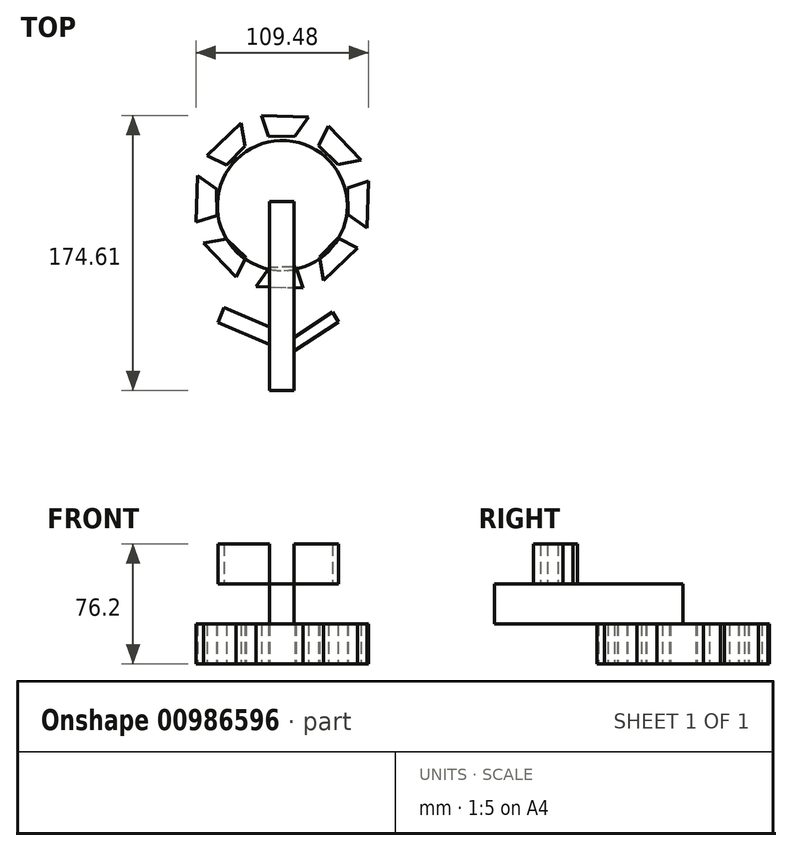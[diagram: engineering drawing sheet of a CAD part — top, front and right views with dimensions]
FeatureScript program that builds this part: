
annotation { "Feature Type Name" : "Feature", "Feature Type Description" : "" }
export const myFeature = defineFeature(function(context is Context, id is Id, definition is map)
    precondition{}
    {
        {
            var Q0;
            Q0=qCreatedBy(makeId("Top.planeOp"),FACE);
            var sketch = newSketch(context, id + "F0", { "sketchPlane" : qUnion([Q0])});
            skCircle(sketch, "E0", {"center": v(0, -2.45) * mm, "radius": 41.29 * mm});
            skSolve(sketch);
        }
        {
            var Q0;
            Q0=qCreatedBy(makeId("Top.planeOp"),FACE);
            var sketch = newSketch(context, id + "F1", { "sketchPlane" : qUnion([Q0])});
            skLineSegment(sketch, "E1", {"start": v(23.17, 35.54) * mm, "end": v(35.26, 23.74) * mm});
            skLineSegment(sketch, "E2", {"start": v(35.26, 23.74) * mm, "end": v(49.93, 26.33) * mm});
            skLineSegment(sketch, "E3", {"start": v(49.93, 26.33) * mm, "end": v(29.5, 47.92) * mm});
            skLineSegment(sketch, "E4", {"start": v(29.5, 47.92) * mm, "end": v(23.17, 35.54) * mm});
            skLineSegment(sketch, "E5.1.0", {"start": v(-13.02, 54.74) * mm, "end": v(-8.75, 41.52) * mm});
            skLineSegment(sketch, "E5.1.1", {"start": v(16.69, 53.93) * mm, "end": v(-13.02, 54.74) * mm});
            skLineSegment(sketch, "E5.1.2", {"start": v(8.14, 41.72) * mm, "end": v(16.69, 53.93) * mm});
            skLineSegment(sketch, "E5.1.3", {"start": v(-8.75, 41.52) * mm, "end": v(8.14, 41.72) * mm});
            skLineSegment(sketch, "E5.2.0", {"start": v(-47.92, 29.5) * mm, "end": v(-35.54, 23.17) * mm});
            skLineSegment(sketch, "E5.2.1", {"start": v(-26.33, 49.93) * mm, "end": v(-47.92, 29.5) * mm});
            skLineSegment(sketch, "E5.2.2", {"start": v(-23.74, 35.26) * mm, "end": v(-26.33, 49.93) * mm});
            skLineSegment(sketch, "E5.2.3", {"start": v(-35.54, 23.17) * mm, "end": v(-23.74, 35.26) * mm});
            skLineSegment(sketch, "E5.3.0", {"start": v(-54.74, -13.02) * mm, "end": v(-41.52, -8.75) * mm});
            skLineSegment(sketch, "E5.3.1", {"start": v(-53.93, 16.69) * mm, "end": v(-54.74, -13.02) * mm});
            skLineSegment(sketch, "E5.3.2", {"start": v(-41.72, 8.14) * mm, "end": v(-53.93, 16.69) * mm});
            skLineSegment(sketch, "E5.3.3", {"start": v(-41.52, -8.75) * mm, "end": v(-41.72, 8.14) * mm});
            skLineSegment(sketch, "E5.4.0", {"start": v(-29.5, -47.92) * mm, "end": v(-23.17, -35.54) * mm});
            skLineSegment(sketch, "E5.4.1", {"start": v(-49.93, -26.33) * mm, "end": v(-29.5, -47.92) * mm});
            skLineSegment(sketch, "E5.4.2", {"start": v(-35.26, -23.74) * mm, "end": v(-49.93, -26.33) * mm});
            skLineSegment(sketch, "E5.4.3", {"start": v(-23.17, -35.54) * mm, "end": v(-35.26, -23.74) * mm});
            skLineSegment(sketch, "E5.5.0", {"start": v(13.02, -54.74) * mm, "end": v(8.75, -41.52) * mm});
            skLineSegment(sketch, "E5.5.1", {"start": v(-16.69, -53.93) * mm, "end": v(13.02, -54.74) * mm});
            skLineSegment(sketch, "E5.5.2", {"start": v(-8.14, -41.72) * mm, "end": v(-16.69, -53.93) * mm});
            skLineSegment(sketch, "E5.5.3", {"start": v(8.75, -41.52) * mm, "end": v(-8.14, -41.72) * mm});
            skLineSegment(sketch, "E5.6.0", {"start": v(47.92, -29.5) * mm, "end": v(35.54, -23.17) * mm});
            skLineSegment(sketch, "E5.6.1", {"start": v(26.33, -49.93) * mm, "end": v(47.92, -29.5) * mm});
            skLineSegment(sketch, "E5.6.2", {"start": v(23.74, -35.26) * mm, "end": v(26.33, -49.93) * mm});
            skLineSegment(sketch, "E5.6.3", {"start": v(35.54, -23.17) * mm, "end": v(23.74, -35.26) * mm});
            skLineSegment(sketch, "E5.7.0", {"start": v(54.74, 13.02) * mm, "end": v(41.52, 8.75) * mm});
            skLineSegment(sketch, "E5.7.1", {"start": v(53.93, -16.69) * mm, "end": v(54.74, 13.02) * mm});
            skLineSegment(sketch, "E5.7.2", {"start": v(41.72, -8.14) * mm, "end": v(53.93, -16.69) * mm});
            skLineSegment(sketch, "E5.7.3", {"start": v(41.52, 8.75) * mm, "end": v(41.72, -8.14) * mm});
            skPoint(sketch, "E5.center", {"position": v(0, 0) * mm});
            skSolve(sketch);
        }
        {
            var Q0;
            Q0=makeQuery(id+"F1.imprint","IMPRINT",FACE,{"disambiguationData":[TD([[makeQuery(id+"F1.imprint","IMPRINT",EDGE,{"derivedFrom":sQuery(id+"F1.wireOp",EDGE,"E5.6.0")}),1.0]])]});
            var Q1;
            Q1=makeQuery(id+"F1.imprint","IMPRINT",FACE,{"disambiguationData":[TD([[makeQuery(id+"F1.imprint","IMPRINT",EDGE,{"derivedFrom":sQuery(id+"F1.wireOp",EDGE,"E5.7.0")}),1.0]])]});
            var Q2;
            Q2=makeQuery(id+"F1.imprint","IMPRINT",FACE,{"disambiguationData":[TD([[makeQuery(id+"F1.imprint","IMPRINT",EDGE,{"derivedFrom":sQuery(id+"F1.wireOp",EDGE,"E5.1.0")}),1.0]])]});
            var Q3;
            Q3=makeQuery(id+"F1.imprint","IMPRINT",FACE,{"disambiguationData":[TD([[makeQuery(id+"F1.imprint","IMPRINT",EDGE,{"derivedFrom":sQuery(id+"F1.wireOp",EDGE,"E5.2.0")}),1.0]])]});
            var Q4;
            Q4=makeQuery(id+"F1.imprint","IMPRINT",FACE,{"disambiguationData":[TD([[makeQuery(id+"F1.imprint","IMPRINT",EDGE,{"derivedFrom":sQuery(id+"F1.wireOp",EDGE,"E5.3.0")}),1.0]])]});
            var Q5;
            Q5=makeQuery(id+"F1.imprint","IMPRINT",FACE,{"disambiguationData":[TD([[makeQuery(id+"F1.imprint","IMPRINT",EDGE,{"derivedFrom":sQuery(id+"F1.wireOp",EDGE,"E5.4.0")}),1.0]])]});
            var Q6;
            Q6=makeQuery(id+"F1.imprint","IMPRINT",FACE,{"disambiguationData":[TD([[makeQuery(id+"F1.imprint","IMPRINT",EDGE,{"derivedFrom":sQuery(id+"F1.wireOp",EDGE,"E5.5.0")}),1.0]])]});
            var Q7;
            Q7=makeQuery(id+"F1.imprint","IMPRINT",FACE,{"disambiguationData":[TD([[makeQuery(id+"F1.imprint","IMPRINT",EDGE,{"derivedFrom":sQuery(id+"F1.wireOp",EDGE,"E1")}),1.0]])]});
            extrude(context, id + "F2", {"entities" : qUnion([Q0, Q1, Q2, Q3, Q4, Q5, Q6, Q7]), "depth" : 25.4 * mm, "offsetDistance" : 25.4 * mm});
        }
        {
            var Q0;
            Q0=makeQuery(id+"F0.imprint","IMPRINT",FACE,{"disambiguationData":[TD([[makeQuery(id+"F0.imprint","IMPRINT",EDGE,{"derivedFrom":sQuery(id+"F0.wireOp",EDGE,"E0")}),1.0]])]});
            extrude(context, id + "F3", {"entities" : qUnion([Q0]), "depth" : 25.4 * mm, "offsetDistance" : 25.4 * mm});
        }
        {
            var Q0;
            Q0=makeQuery(id+"F3.opExtrude","CAP_FACE",FACE,{"disambiguationData":[OSD([sQuery(id+"F0.wireOp",EDGE,"E0")])],"isStart":false});
            var sketch = newSketch(context, id + "F4", { "sketchPlane" : qUnion([Q0])});
            skLineSegment(sketch, "E6", {"start": v(-8.1, 0) * mm, "end": v(-8.1, -119.87) * mm});
            skLineSegment(sketch, "E7", {"start": v(-8.1, -119.87) * mm, "end": v(7.44, -119.87) * mm});
            skLineSegment(sketch, "E8", {"start": v(7.44, -119.87) * mm, "end": v(7.44, 0) * mm});
            skLineSegment(sketch, "E9", {"start": v(7.44, 0) * mm, "end": v(-8.1, 0) * mm});
            skSolve(sketch);
        }
        {
            var Q0;
            Q0 = qSketchRegion(id + "F4", true);
            extrude(context, id + "F5", {"entities" : qUnion([Q0]), "depth" : 25.4 * mm, "offsetDistance" : 25.4 * mm});
        }
        {
            var Q0;
            Q0=makeQuery(id+"F5.opExtrude","CAP_FACE",FACE,{"disambiguationData":[OSD([sQuery(id+"F4.wireOp",EDGE,"E6"),sQuery(id+"F4.wireOp",EDGE,"E7"),sQuery(id+"F4.wireOp",EDGE,"E8"),sQuery(id+"F4.wireOp",EDGE,"E9")])],"isStart":false});
            var sketch = newSketch(context, id + "F6", { "sketchPlane" : qUnion([Q0])});
            skLineSegment(sketch, "E10", {"start": v(7.44, -86.11) * mm, "end": v(31.75, -70.14) * mm});
            skLineSegment(sketch, "E11", {"start": v(31.75, -70.14) * mm, "end": v(35.8, -76.3) * mm});
            skLineSegment(sketch, "E12", {"start": v(35.8, -76.3) * mm, "end": v(7.44, -94.93) * mm});
            skLineSegment(sketch, "E13", {"start": v(7.44, -94.93) * mm, "end": v(7.44, -86.11) * mm});
            skLineSegment(sketch, "E14", {"start": v(-8.1, -79.41) * mm, "end": v(-36.84, -67.2) * mm});
            skLineSegment(sketch, "E15", {"start": v(-36.84, -67.2) * mm, "end": v(-40.84, -76.6) * mm});
            skLineSegment(sketch, "E16", {"start": v(-40.84, -76.6) * mm, "end": v(-8.1, -90.52) * mm});
            skPoint(sketch, "E16.endSnap0", {"position": v(7.44, -90.52) * mm});
            skLineSegment(sketch, "E17", {"start": v(-8.1, -90.52) * mm, "end": v(-8.1, -79.41) * mm});
            skSolve(sketch);
        }
        {
            var Q0;
            Q0 = qSketchRegion(id + "F6", true);
            extrude(context, id + "F7", {"entities" : qUnion([Q0]), "depth" : 25.4 * mm, "offsetDistance" : 25.4 * mm});
        }
    });
